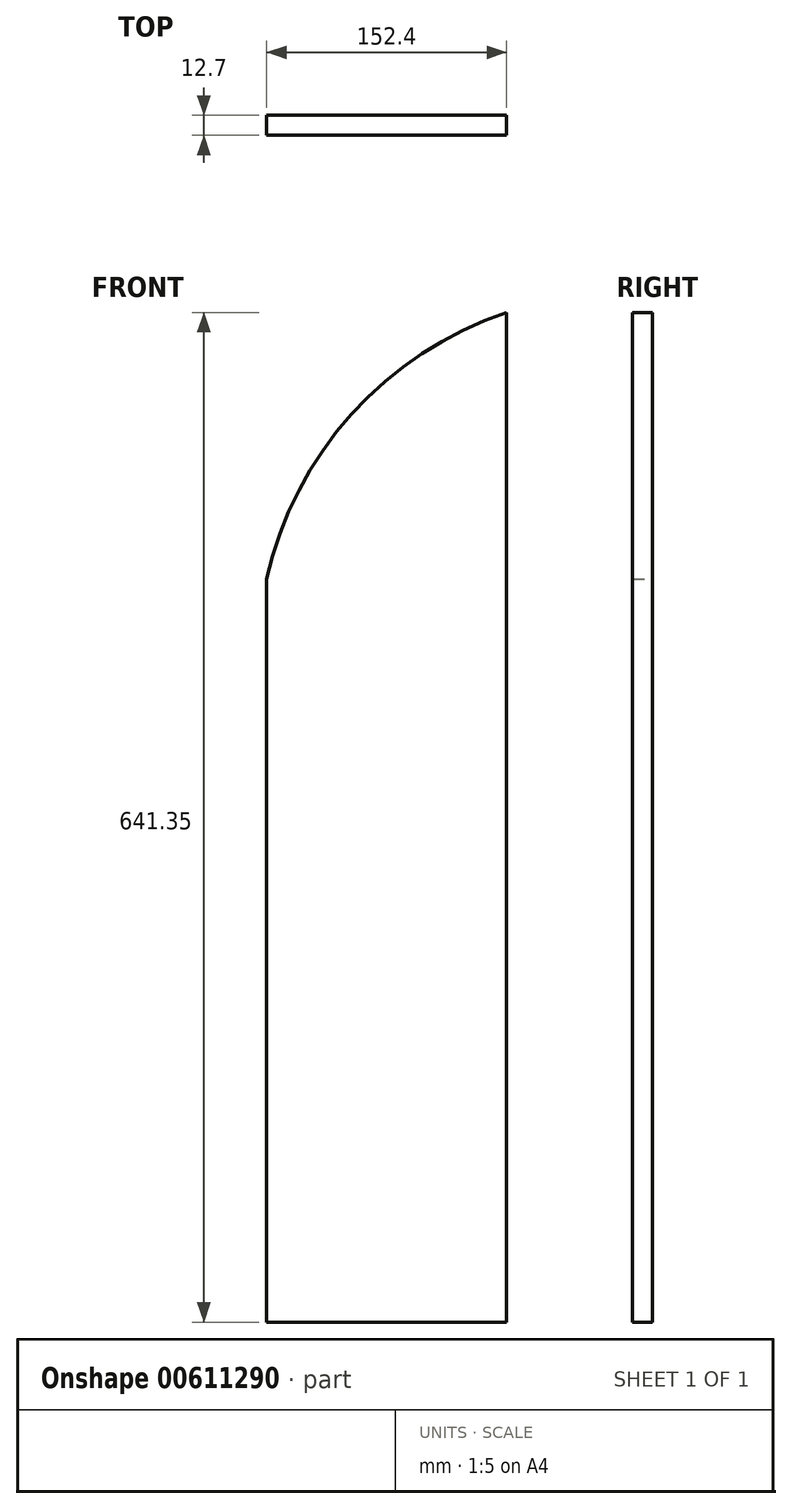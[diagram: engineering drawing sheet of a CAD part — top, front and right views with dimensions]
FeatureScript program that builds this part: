
annotation { "Feature Type Name" : "Feature", "Feature Type Description" : "" }
export const myFeature = defineFeature(function(context is Context, id is Id, definition is map)
    precondition{}
    {
        {
            var Q0;
            Q0=qCreatedBy(makeId("Front.planeOp"),FACE);
            var sketch = newSketch(context, id + "F0", { "sketchPlane" : qUnion([Q0])});
            skLineSegment(sketch, "E0.top", {"start": v(-225.68, -308.73) * mm, "end": v(-73.28, -308.73) * mm});
            skLineSegment(sketch, "E0.left", {"start": v(-225.68, 163.36) * mm, "end": v(-225.68, -308.73) * mm});
            skLineSegment(sketch, "E0.right", {"start": v(-73.28, 332.62) * mm, "end": v(-73.28, -308.73) * mm});
            skArc(sketch, "E1", {"start": v(-73.28, 332.62) * mm, "mid": v(-171.78, 268.07) * mm, "end": v(-225.68, 163.36) * mm});
            skSolve(sketch);
        }
        {
            var Q0;
            Q0 = qSketchRegion(id + "F0", true);
            extrude(context, id + "F1", {"entities" : qUnion([Q0]), "depth" : 12.7 * mm, "offsetDistance" : 25.4 * mm});
        }
    });
